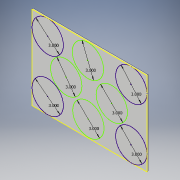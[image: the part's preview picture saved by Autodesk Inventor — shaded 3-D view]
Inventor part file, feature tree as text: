
AUTODESK INVENTOR PART (.ipt)
format: ipt  version: 2017 (Build 210142000, 142)  size: 104,960 bytes
history: native  units: in
note: dims shown in document units (in); Inventor stores cm internally (conversion verified against a paired STEP export)
features: sketch x2, extrude x1
ambient origin geometry x8: Origin, YZ Plane, XZ Plane, XY Plane, X Axis, Y Axis, Z Axis, Center Point
bodies: Solid1 (feature_tree)
feature tree (3):
  extrude  "Extrusion1"  Depth=8.0in
  sketch  "Sketch2"  dims[d2=0.125in d3=0.0in d4=3.0in d5=3.0in d6=3.0in d7=3.0in d8=3.0in d9=3.0in d10=3.0in d11=3.0in]
  sketch  "Sketch1"  dims[d0=11.0in d1=8.0in]
